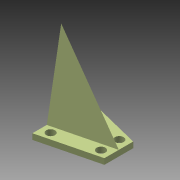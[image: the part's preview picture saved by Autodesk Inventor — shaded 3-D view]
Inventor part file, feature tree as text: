
AUTODESK INVENTOR PART (.ipt)
format: ipt  version: 2015 (Build 190159000, 159)  size: 114,176 bytes
history: native  units: mm
features: sketch x4, extrude x2, loft x1, shell x1
ambient origin geometry x8: Origin, YZ Plane, XZ Plane, XY Plane, X Axis, Y Axis, Z Axis, Center Point
bodies: 实体1 (feature_tree)
feature tree (8):
  loft  "放样1"
  shell  "抽壳1"  Thickness=28.0mm
  extrude  "拉伸1"  TaperAngle=0.0deg  [1 undecoded]
  extrude  "拉伸2"  Depth=20.0mm
  sketch  "草图1"  dims[d0=10.0mm d1=20.0mm d2=28.0mm]
  sketch  "草图2"  dims[d3=0.0mm d4=90.0deg d5=0.0mm d6=90.0deg]
  sketch  "草图3"  dims[d7=1.0mm d8=20.0mm]
  sketch  "草图4"  dims[d9=2.0mm d10=0.0mm d11=3.0mm d12=2.5mm d13=3.0mm d14=3.0mm d15=3.0mm d16=2.5mm d17=2.5mm d18=2.5mm d19=3.0mm d20=3.0mm d21=3.0mm d22=3.0mm d23=2.0mm d24=0.0mm]
note: 1 required parameter value undecoded (feature->parameter linkage not recoverable at this tier; creation-order binding heuristic only, values carry confidence <= 0.55)
